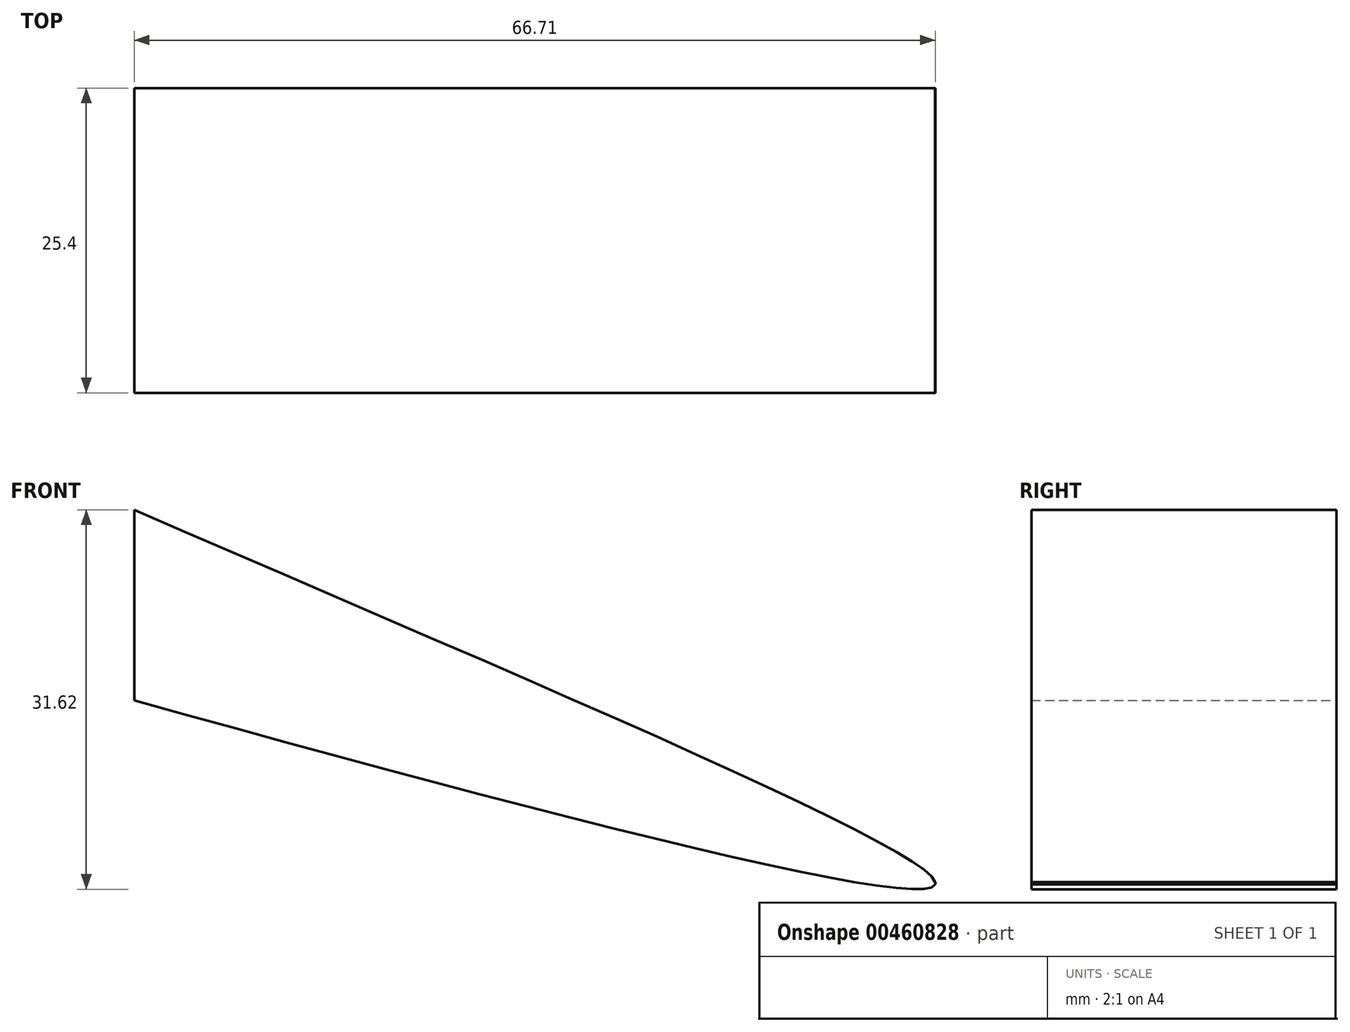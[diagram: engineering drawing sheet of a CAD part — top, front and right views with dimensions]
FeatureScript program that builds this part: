
annotation { "Feature Type Name" : "Feature", "Feature Type Description" : "" }
export const myFeature = defineFeature(function(context is Context, id is Id, definition is map)
    precondition{}
    {
        {
            var Q0;
            Q0=qCreatedBy(makeId("Front.planeOp"),FACE);
            var sketch = newSketch(context, id + "F0", { "sketchPlane" : qUnion([Q0])});
            skFitSpline(sketch, "E0", {"points": [v(-38.38, 31.23) * mm, v(28.32, 0) * mm, v(-38.38, 15.36) * mm], "startDerivative": vector(196.2, -84.98) * mm, "endDerivative": vector(-196.9, 55.22) * mm});
            skLineSegment(sketch, "E1", {"start": v(28.32, 0) * mm, "end": v(28.32, 32.86) * mm});
            skLineSegment(sketch, "E2", {"start": v(-38.38, 25.1) * mm, "end": v(-38.38, 0) * mm});
            skLineSegment(sketch, "E3", {"start": v(-38.38, 0) * mm, "end": v(-38.38, 46.92) * mm});
            skSolve(sketch);
        }
        {
            var Q0;
            Q0 = qSketchRegion(id + "F0", true);
            extrude(context, id + "F1", {"entities" : qUnion([Q0]), "depth" : 25.4 * mm});
        }
    });
